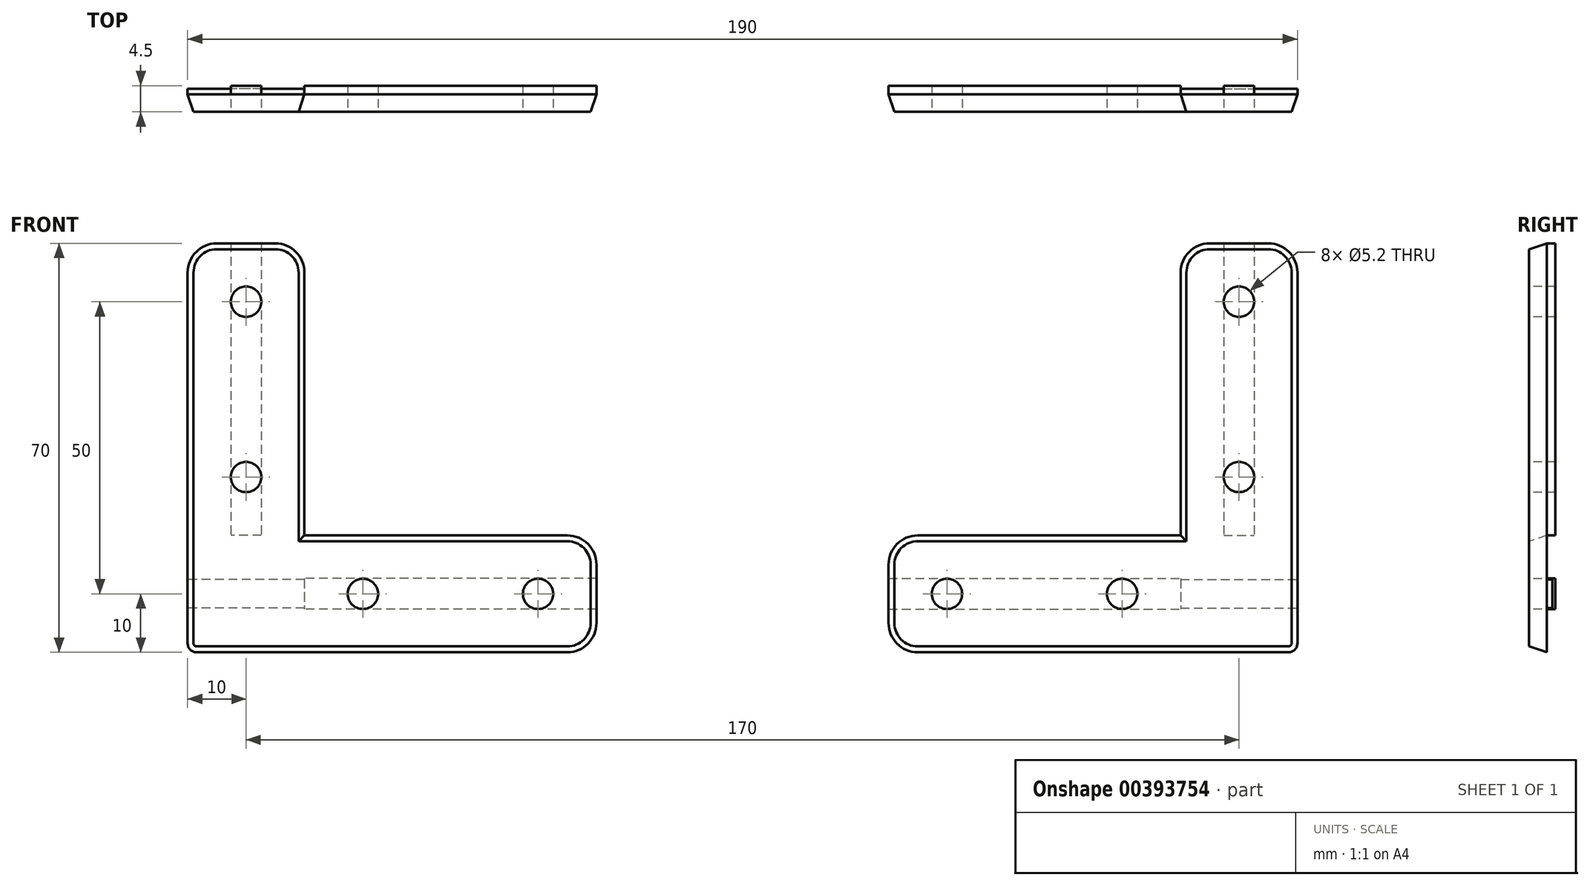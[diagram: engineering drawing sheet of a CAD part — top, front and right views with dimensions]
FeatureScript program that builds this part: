
annotation { "Feature Type Name" : "Feature", "Feature Type Description" : "" }
export const myFeature = defineFeature(function(context is Context, id is Id, definition is map)
    precondition{}
    {
        {
            var Q0;
            Q0=qCreatedBy(makeId("Front.planeOp"),FACE);
            var sketch = newSketch(context, id + "F0", { "sketchPlane" : qUnion([Q0])});
            skLineSegment(sketch, "E0", {"start": v(0, 1.52) * mm, "end": v(0, 65) * mm});
            skLineSegment(sketch, "E1", {"start": v(-70, 15) * mm, "end": v(-70, 5) * mm});
            skLineSegment(sketch, "E2", {"start": v(-65, 0) * mm, "end": v(-1.52, 0) * mm});
            skLineSegment(sketch, "E3", {"start": v(-65, 20) * mm, "end": v(-20, 20) * mm});
            skLineSegment(sketch, "E4", {"start": v(-5, 70) * mm, "end": v(-15, 70) * mm});
            skLineSegment(sketch, "E5", {"start": v(-20, 65) * mm, "end": v(-20, 20) * mm});
            skPoint(sketch, "E6.visualSharp", {"position": v(0, 0) * mm});
            skArc(sketch, "E6.filletArc", {"start": v(-1.52, 0) * mm, "mid": v(-0.44, 0.44) * mm, "end": v(0, 1.51) * mm});
            skPoint(sketch, "E7.visualSharp", {"position": v(0, 70) * mm});
            skArc(sketch, "E7.filletArc", {"start": v(0, 65) * mm, "mid": v(-1.46, 68.54) * mm, "end": v(-5, 70) * mm});
            skPoint(sketch, "E8.visualSharp", {"position": v(-20, 70) * mm});
            skArc(sketch, "E8.filletArc", {"start": v(-15, 70) * mm, "mid": v(-18.54, 68.54) * mm, "end": v(-20, 65) * mm});
            skPoint(sketch, "E9.visualSharp", {"position": v(-70, 20) * mm});
            skArc(sketch, "E9.filletArc", {"start": v(-65, 20) * mm, "mid": v(-68.54, 18.54) * mm, "end": v(-70, 15) * mm});
            skPoint(sketch, "E10.visualSharp", {"position": v(-70, 0) * mm});
            skArc(sketch, "E10.filletArc", {"start": v(-70, 5) * mm, "mid": v(-68.54, 1.46) * mm, "end": v(-65, 0) * mm});
            skPoint(sketch, "E11", {"position": v(-10, 60) * mm});
            skPoint(sketch, "E12", {"position": v(-10, 30) * mm});
            skPoint(sketch, "E13", {"position": v(-30, 10) * mm});
            skPoint(sketch, "E14", {"position": v(-60, 10) * mm});
            skSolve(sketch);
        }
        {
            var Q0;
            Q0 = qSketchRegion(id + "F0", true);
            extrude(context, id + "F1", {"entities" : qUnion([Q0]), "depth" : 3 * mm});
        }
        {
            var Q0;
            Q0=makeQuery(id+"F1.opExtrude","SWEPT_FACE",FACE,{"disambiguationData":[OSD([sQuery(id+"F0.wireOp",EDGE,"E0")])]});
            var sketch = newSketch(context, id + "F2", { "sketchPlane" : qUnion([Q0])});
            skPoint(sketch, "E15", {"position": v(0, 10) * mm});
            skLineSegment(sketch, "E16.0", {"start": v(0, 12.43) * mm, "end": v(1, 12.43) * mm});
            skLineSegment(sketch, "E17.0", {"start": v(1, 7.57) * mm, "end": v(0, 7.57) * mm});
            skLineSegment(sketch, "E18", {"start": v(0, 7.57) * mm, "end": v(0, 12.43) * mm});
            skLineSegment(sketch, "E19", {"start": v(1, 12.43) * mm, "end": v(1, 7.57) * mm});
            skSolve(sketch);
        }
        {
            var Q0;
            Q0 = qSketchRegion(id + "F2", true);
            extrude(context, id + "F3", {"entities" : qUnion([Q0]), "operationType" : NewBodyOperationType.ADD, "oppositeDirection" : true, "depth" : 20 * mm});
        }
        {
            var Q0;
            Q0=makeQuery(id+"F1.opExtrude","CAP_FACE",FACE,{"disambiguationData":[OSD([sQuery(id+"F0.wireOp",EDGE,"E0"),sQuery(id+"F0.wireOp",EDGE,"E1"),sQuery(id+"F0.wireOp",EDGE,"E2"),sQuery(id+"F0.wireOp",EDGE,"1116788b-cc91-41a3-8a37-d864bfd44548"),sQuery(id+"F0.wireOp",EDGE,"b9222880-3f47-49a7-a3aa-43686d3323fb"),sQuery(id+"F0.wireOp",EDGE,"2c049e49-2f2e-4a62-95ef-4c59848bfe10"),sQuery(id+"F0.wireOp",EDGE,"40b9bb01-7986-4d4f-9e53-eeab950f5564"),sQuery(id+"F0.wireOp",EDGE,"E3"),sQuery(id+"F0.wireOp",EDGE,"E4"),sQuery(id+"F0.wireOp",EDGE,"E5"),sQuery(id+"F0.wireOp",EDGE,"E6.filletArc"),sQuery(id+"F0.wireOp",EDGE,"E7.filletArc"),sQuery(id+"F0.wireOp",EDGE,"E8.filletArc"),sQuery(id+"F0.wireOp",EDGE,"E9.filletArc"),sQuery(id+"F0.wireOp",EDGE,"E10.filletArc")])],"isStart":true});
            var sketch = newSketch(context, id + "F4", { "sketchPlane" : qUnion([Q0])});
            skLineSegment(sketch, "E20.bottom", {"start": v(12.63, 70) * mm, "end": v(7.38, 70) * mm});
            skLineSegment(sketch, "E20.top", {"start": v(12.63, 20) * mm, "end": v(7.38, 20) * mm});
            skLineSegment(sketch, "E20.left", {"start": v(12.63, 70) * mm, "end": v(12.63, 20) * mm});
            skLineSegment(sketch, "E20.right", {"start": v(7.38, 70) * mm, "end": v(7.38, 20) * mm});
            skPoint(sketch, "E20.middle", {"position": v(10, 45) * mm});
            skLineSegment(sketch, "E21.bottom", {"start": v(70, 12.63) * mm, "end": v(20, 12.63) * mm});
            skLineSegment(sketch, "E21.top", {"start": v(70, 7.38) * mm, "end": v(20, 7.38) * mm});
            skLineSegment(sketch, "E21.left", {"start": v(70, 12.63) * mm, "end": v(70, 7.38) * mm});
            skLineSegment(sketch, "E21.right", {"start": v(20, 12.63) * mm, "end": v(20, 7.38) * mm});
            skPoint(sketch, "E21.middle", {"position": v(45, 10) * mm});
            skSolve(sketch);
        }
        {
            var Q0;
            Q0 = qSketchRegion(id + "F4", true);
            extrude(context, id + "F5", {"entities" : qUnion([Q0]), "operationType" : NewBodyOperationType.ADD, "depth" : 1.5 * mm});
        }
        {
            var Q0;
            Q0=makeQuery(id+"F1.opExtrude","CAP_FACE",FACE,{"disambiguationData":[OSD([sQuery(id+"F0.wireOp",EDGE,"E0"),sQuery(id+"F0.wireOp",EDGE,"E1"),sQuery(id+"F0.wireOp",EDGE,"E2"),sQuery(id+"F0.wireOp",EDGE,"E3"),sQuery(id+"F0.wireOp",EDGE,"E4"),sQuery(id+"F0.wireOp",EDGE,"E5"),sQuery(id+"F0.wireOp",EDGE,"E6.filletArc"),sQuery(id+"F0.wireOp",EDGE,"E7.filletArc"),sQuery(id+"F0.wireOp",EDGE,"E8.filletArc"),sQuery(id+"F0.wireOp",EDGE,"E9.filletArc"),sQuery(id+"F0.wireOp",EDGE,"E10.filletArc")])],"isStart":false});
            var sketch = newSketch(context, id + "F6", { "sketchPlane" : qUnion([Q0])});
            skCircle(sketch, "E22", {"center": v(-10, 60) * mm, "radius": 2.6 * mm});
            skCircle(sketch, "E23", {"center": v(-10, 30) * mm, "radius": 2.6 * mm});
            skCircle(sketch, "E24", {"center": v(-30, 10) * mm, "radius": 2.6 * mm});
            skCircle(sketch, "E25", {"center": v(-60, 10) * mm, "radius": 2.6 * mm});
            skSolve(sketch);
        }
        {
            var Q0;
            Q0 = qSketchRegion(id + "F6", true);
            extrude(context, id + "F7", {"entities" : qUnion([Q0]), "operationType" : NewBodyOperationType.REMOVE, "endBound" : BoundingType.THROUGH_ALL, "oppositeDirection" : true, "depth" : 25 * mm});
        }
        {
            var Q0;
            Q0=makeQuery(id+"F5.boolean.opBoolean","MERGE",FACE,{"derivedFrom":[makeQuery(id+"F1.opExtrude","SWEPT_FACE",FACE,{"disambiguationData":[OSD([sQuery(id+"F0.wireOp",EDGE,"E1")])]}),makeQuery(id+"F5.opExtrude","SWEPT_FACE",FACE,{"disambiguationData":[OSD([sQuery(id+"F4.wireOp",EDGE,"E21.left")])]})]});
            cPlane(context, id + "F8", {"entities" : qUnion([Q0]), "cplaneType" : CPlaneType.OFFSET, "offset" : 25 * mm, "width" : 150 * mm, "height" : 150 * mm});
        }
        {
            var Q0;
            Q0=makeQuery(id+"F1.opExtrude","CAP_EDGE",EDGE,{"disambiguationData":[OSD([sQuery(id+"F0.wireOp",EDGE,"E3")])],"isStart":false});
            chamfer(context, id + "F9", {"entities" : qUnion([Q0]), "chamferType" : ChamferType.TWO_OFFSETS, "width1" : 3 * mm, "oppositeDirection" : false, "width2" : 1 * mm, "tangentPropagation" : true});
        }
        {
            var Q0;
            Q0=makeQuery(id+"F1.opExtrude","SWEPT_BODY",BODY,{"disambiguationData":[OSD([sQuery(id+"F0.wireOp",EDGE,"E0"),sQuery(id+"F0.wireOp",EDGE,"E1"),sQuery(id+"F0.wireOp",EDGE,"E2"),sQuery(id+"F0.wireOp",EDGE,"E3"),sQuery(id+"F0.wireOp",EDGE,"E4"),sQuery(id+"F0.wireOp",EDGE,"E5"),sQuery(id+"F0.wireOp",EDGE,"E6.filletArc"),sQuery(id+"F0.wireOp",EDGE,"E7.filletArc"),sQuery(id+"F0.wireOp",EDGE,"E8.filletArc"),sQuery(id+"F0.wireOp",EDGE,"E9.filletArc"),sQuery(id+"F0.wireOp",EDGE,"E10.filletArc")])]});
            var Q1;
            Q1=qCreatedBy(id+"F8.planeOp",FACE);
            mirror(context, id + "F10", {"entities" : qUnion([Q0]), "mirrorPlane" : qUnion([Q1])});
        }
    });
